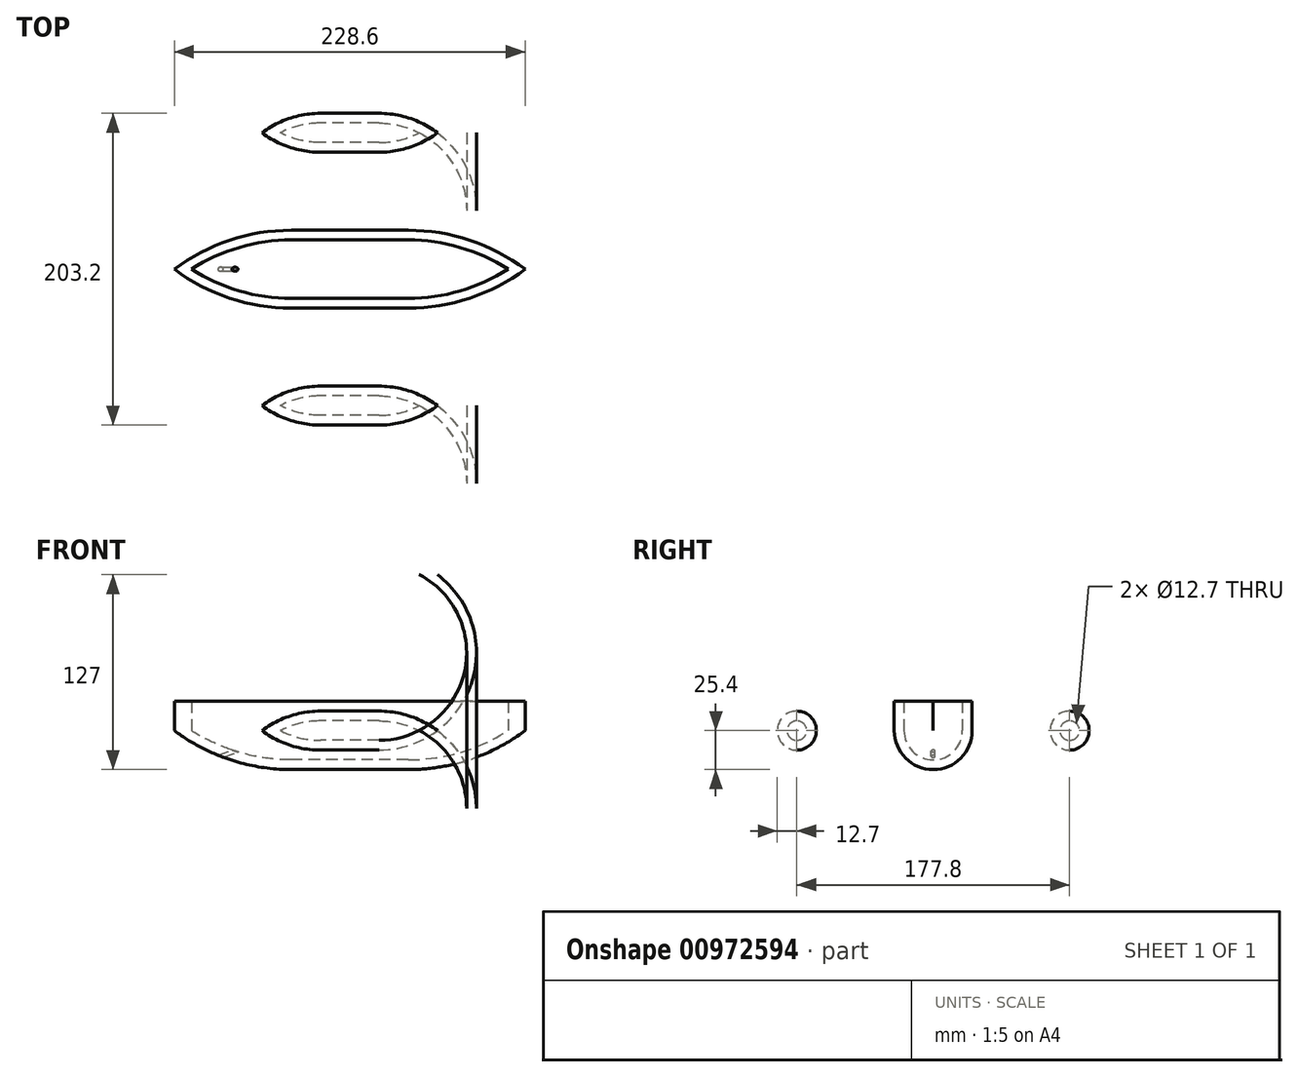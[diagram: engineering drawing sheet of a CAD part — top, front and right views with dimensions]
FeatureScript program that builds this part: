
annotation { "Feature Type Name" : "Feature", "Feature Type Description" : "" }
export const myFeature = defineFeature(function(context is Context, id is Id, definition is map)
    precondition{}
    {
        {
            var Q0;
            Q0=qCreatedBy(makeId("Top.planeOp"),FACE);
            var sketch = newSketch(context, id + "F0", { "sketchPlane" : qUnion([Q0])});
            skLineSegment(sketch, "E0.bottom", {"start": v(-38.1, 25.4) * mm, "end": v(38.1, 25.4) * mm});
            skLineSegment(sketch, "E0.top", {"start": v(-38.1, -25.4) * mm, "end": v(38.1, -25.4) * mm});
            skLineSegment(sketch, "E0.left", {"start": v(-38.1, 25.4) * mm, "end": v(-38.1, -25.4) * mm});
            skLineSegment(sketch, "E0.right", {"start": v(38.1, 25.4) * mm, "end": v(38.1, -25.4) * mm});
            skPoint(sketch, "E1", {"position": v(0, 25.4) * mm});
            skPoint(sketch, "E2", {"position": v(-38.1, 0) * mm});
            skLineSegment(sketch, "E3", {"start": v(-38.1, 0) * mm, "end": v(-114.3, 0) * mm});
            skLineSegment(sketch, "E4", {"start": v(38.1, 0) * mm, "end": v(114.3, 0) * mm});
            skArc(sketch, "E5", {"start": v(-38.1, 25.4) * mm, "mid": v(-78.26, 18.88) * mm, "end": v(-114.3, 0) * mm});
            skArc(sketch, "E6", {"start": v(-114.3, 0) * mm, "mid": v(-78.26, -18.88) * mm, "end": v(-38.1, -25.4) * mm});
            skArc(sketch, "E7", {"start": v(114.3, 0) * mm, "mid": v(78.26, 18.88) * mm, "end": v(38.1, 25.4) * mm});
            skArc(sketch, "E8", {"start": v(38.1, -25.4) * mm, "mid": v(78.26, -18.88) * mm, "end": v(114.3, 0) * mm});
            skArc(sketch, "E9.0", {"start": v(-38.1, 19.05) * mm, "mid": v(-72, 14.19) * mm, "end": v(-103.17, 0) * mm});
            skArc(sketch, "E9.1", {"start": v(103.17, 0) * mm, "mid": v(72, 14.19) * mm, "end": v(38.1, 19.05) * mm});
            skArc(sketch, "E9.2", {"start": v(38.1, -19.05) * mm, "mid": v(72, -14.19) * mm, "end": v(103.17, 0) * mm});
            skLineSegment(sketch, "E9.3", {"start": v(-38.1, 19.05) * mm, "end": v(38.1, 19.05) * mm});
            skLineSegment(sketch, "E9.4", {"start": v(-38.1, -19.05) * mm, "end": v(38.1, -19.05) * mm});
            skArc(sketch, "E9.5", {"start": v(-103.17, 0) * mm, "mid": v(-72, -14.19) * mm, "end": v(-38.1, -19.05) * mm});
            skLineSegment(sketch, "E10.bottom", {"start": v(-19.05, 101.6) * mm, "end": v(19.05, 101.6) * mm});
            skLineSegment(sketch, "E10.top", {"start": v(-19.05, 76.2) * mm, "end": v(19.05, 76.2) * mm});
            skLineSegment(sketch, "E10.left", {"start": v(-19.05, 101.6) * mm, "end": v(-19.05, 76.2) * mm});
            skLineSegment(sketch, "E10.right", {"start": v(19.05, 101.6) * mm, "end": v(19.05, 76.2) * mm});
            skPoint(sketch, "E11", {"position": v(0, 76.2) * mm});
            skLineSegment(sketch, "E12", {"start": v(-19.05, 88.9) * mm, "end": v(-57.15, 88.9) * mm});
            skLineSegment(sketch, "E13", {"start": v(19.05, 88.9) * mm, "end": v(57.15, 88.9) * mm});
            skArc(sketch, "E14", {"start": v(-19.05, 101.6) * mm, "mid": v(-39.13, 98.34) * mm, "end": v(-57.15, 88.9) * mm});
            skArc(sketch, "E15", {"start": v(-57.15, 88.9) * mm, "mid": v(-39.13, 79.46) * mm, "end": v(-19.05, 76.2) * mm});
            skArc(sketch, "E16", {"start": v(57.15, 88.9) * mm, "mid": v(39.13, 98.34) * mm, "end": v(19.05, 101.6) * mm});
            skArc(sketch, "E17", {"start": v(19.05, 76.2) * mm, "mid": v(39.13, 79.46) * mm, "end": v(57.15, 88.9) * mm});
            skArc(sketch, "E18.0", {"start": v(-45.23, 88.9) * mm, "mid": v(-32.52, 84.16) * mm, "end": v(-19.05, 82.55) * mm});
            skArc(sketch, "E18.1", {"start": v(19.05, 82.55) * mm, "mid": v(32.52, 84.16) * mm, "end": v(45.23, 88.9) * mm});
            skArc(sketch, "E18.2", {"start": v(45.23, 88.9) * mm, "mid": v(32.52, 93.64) * mm, "end": v(19.05, 95.25) * mm});
            skLineSegment(sketch, "E18.3", {"start": v(-19.05, 82.55) * mm, "end": v(19.05, 82.55) * mm});
            skLineSegment(sketch, "E18.4", {"start": v(-19.05, 95.25) * mm, "end": v(19.05, 95.25) * mm});
            skArc(sketch, "E18.5", {"start": v(-19.05, 95.25) * mm, "mid": v(-32.52, 93.64) * mm, "end": v(-45.23, 88.9) * mm});
            skSolve(sketch);
        }
        {
            var Q0;
            {var subQ0=sQuery(id+"F0.wireOp",EDGE,"E5");Q0=makeQuery(id+"F0.imprint","IMPRINT",FACE,{"disambiguationData":[TD([[makeQuery(id+"F0.imprint","IMPRINT",EDGE,{"derivedFrom":subQ0}),1.0]])]});}
            var Q1;
            {var subQ0=sQuery(id+"F0.wireOp",EDGE,"E0.bottom");Q1=makeQuery(id+"F0.imprint","IMPRINT",FACE,{"disambiguationData":[TD([[makeQuery(id+"F0.imprint","IMPRINT",EDGE,{"derivedFrom":subQ0}),-1.0]])]});}
            var Q2;
            {var subQ0=sQuery(id+"F0.wireOp",EDGE,"E7");Q2=makeQuery(id+"F0.imprint","IMPRINT",FACE,{"disambiguationData":[TD([[makeQuery(id+"F0.imprint","IMPRINT",EDGE,{"derivedFrom":subQ0}),1.0]])]});}
            var Q3;
            {var subQ0=sQuery(id+"F0.wireOp",EDGE,"E8");Q3=makeQuery(id+"F0.imprint","IMPRINT",FACE,{"disambiguationData":[TD([[makeQuery(id+"F0.imprint","IMPRINT",EDGE,{"derivedFrom":subQ0}),1.0]])]});}
            var Q4;
            {var subQ0=sQuery(id+"F0.wireOp",EDGE,"E0.top");Q4=makeQuery(id+"F0.imprint","IMPRINT",FACE,{"disambiguationData":[TD([[makeQuery(id+"F0.imprint","IMPRINT",EDGE,{"derivedFrom":subQ0}),1.0]])]});}
            var Q5;
            {var subQ0=sQuery(id+"F0.wireOp",EDGE,"E6");Q5=makeQuery(id+"F0.imprint","IMPRINT",FACE,{"disambiguationData":[TD([[makeQuery(id+"F0.imprint","IMPRINT",EDGE,{"derivedFrom":subQ0}),1.0]])]});}
            extrude(context, id + "F1", {"entities" : qUnion([Q0, Q1, Q2, Q3, Q4, Q5]), "depth" : 19.05 * mm, "offsetDistance" : 25.4 * mm});
        }
        {
            var Q0;
            {var subQ0=sQuery(id+"F0.wireOp",EDGE,"E0.top");Q0=makeQuery(id+"F0.imprint","IMPRINT",FACE,{"disambiguationData":[TD([[makeQuery(id+"F0.imprint","IMPRINT",EDGE,{"derivedFrom":subQ0}),1.0]])]});}
            var Q1;
            {var subQ0=sQuery(id+"F0.wireOp",EDGE,"E6");Q1=makeQuery(id+"F0.imprint","IMPRINT",FACE,{"disambiguationData":[TD([[makeQuery(id+"F0.imprint","IMPRINT",EDGE,{"derivedFrom":subQ0}),1.0]])]});}
            var Q2;
            {var subQ0=sQuery(id+"F0.wireOp",EDGE,"E8");Q2=makeQuery(id+"F0.imprint","IMPRINT",FACE,{"disambiguationData":[TD([[makeQuery(id+"F0.imprint","IMPRINT",EDGE,{"derivedFrom":subQ0}),1.0]])]});}
            var Q3;
            Q3=sQuery(id+"F0.wireOp",EDGE,"E3");
            revolve(context, id + "F2", {"operationType" : NewBodyOperationType.ADD, "surfaceOperationType" : NewSurfaceOperationType.NEW, "entities" : qUnion([Q0, Q1, Q2]), "axis" : qUnion([Q3]), "revolveType" : RevolveType.ONE_DIRECTION, "oppositeDirection" : true, "angle" : 180 * degree});
        }
        {
            var Q0;
            Q0=sQuery(id+"F0.wireOp",EDGE,"E0.left");
            cPlane(context, id + "F3", {"entities" : qUnion([Q0]), "cplaneType" : CPlaneType.LINE_ANGLE, "offset" : 25.4 * mm, "angle" : 70 * degree, "oppositeDirection" : true, "width" : 152.4 * mm, "height" : 152.4 * mm});
        }
        {
            var Q0;
            Q0=qCreatedBy(id+"F3.planeOp",FACE);
            var sketch = newSketch(context, id + "F4", { "sketchPlane" : qUnion([Q0])});
            skPoint(sketch, "E19", {"position": v(0, 13.03) * mm});
            skCircle(sketch, "E20", {"center": v(0, 13.03) * mm, "radius": 1.27 * mm});
            skSolve(sketch);
        }
        {
            var Q0;
            Q0=makeQuery(id+"F4.imprint","IMPRINT",FACE,{"disambiguationData":[TD([[makeQuery(id+"F4.imprint","IMPRINT",EDGE,{"derivedFrom":sQuery(id+"F4.wireOp",EDGE,"E20")}),1.0]])]});
            extrude(context, id + "F5", {"entities" : qUnion([Q0]), "operationType" : NewBodyOperationType.REMOVE, "endBound" : BoundingType.THROUGH_ALL, "depth" : 25.4 * mm, "offsetDistance" : 25.4 * mm});
        }
        {
            var Q0;
            {var subQ0=sQuery(id+"F0.wireOp",EDGE,"E15");Q0=makeQuery(id+"F0.imprint","IMPRINT",FACE,{"disambiguationData":[TD([[makeQuery(id+"F0.imprint","IMPRINT",EDGE,{"derivedFrom":subQ0}),1.0]])]});}
            var Q1;
            {var subQ0=sQuery(id+"F0.wireOp",EDGE,"E10.top");Q1=makeQuery(id+"F0.imprint","IMPRINT",FACE,{"disambiguationData":[TD([[makeQuery(id+"F0.imprint","IMPRINT",EDGE,{"derivedFrom":subQ0}),1.0]])]});}
            var Q2;
            {var subQ0=sQuery(id+"F0.wireOp",EDGE,"E17");Q2=makeQuery(id+"F0.imprint","IMPRINT",FACE,{"disambiguationData":[TD([[makeQuery(id+"F0.imprint","IMPRINT",EDGE,{"derivedFrom":subQ0}),1.0]])]});}
            var Q3;
            Q3=sQuery(id+"F0.wireOp",EDGE,"E13");
            revolve(context, id + "F6", {"operationType" : NewBodyOperationType.ADD, "surfaceOperationType" : NewSurfaceOperationType.NEW, "entities" : qUnion([Q0, Q1, Q2]), "axis" : qUnion([Q3]), "revolveType" : RevolveType.FULL});
        }
        {
            var Q0;
            Q0=makeQuery(id+"F6.opRevolve","SWEPT_BODY",BODY,{"disambiguationData":[OSD([sQuery(id+"F0.wireOp",EDGE,"E10.top"),sQuery(id+"F0.wireOp",EDGE,"E12"),sQuery(id+"F0.wireOp",EDGE,"E13"),sQuery(id+"F0.wireOp",EDGE,"E15"),sQuery(id+"F0.wireOp",EDGE,"E17"),sQuery(id+"F0.wireOp",EDGE,"E18.0"),sQuery(id+"F0.wireOp",EDGE,"E18.1"),sQuery(id+"F0.wireOp",EDGE,"E18.3")])]});
            var Q1;
            Q1=qCreatedBy(makeId("Front.planeOp"),FACE);
            mirror(context, id + "F7", {"entities" : qUnion([Q0]), "mirrorPlane" : qUnion([Q1])});
        }
    });
